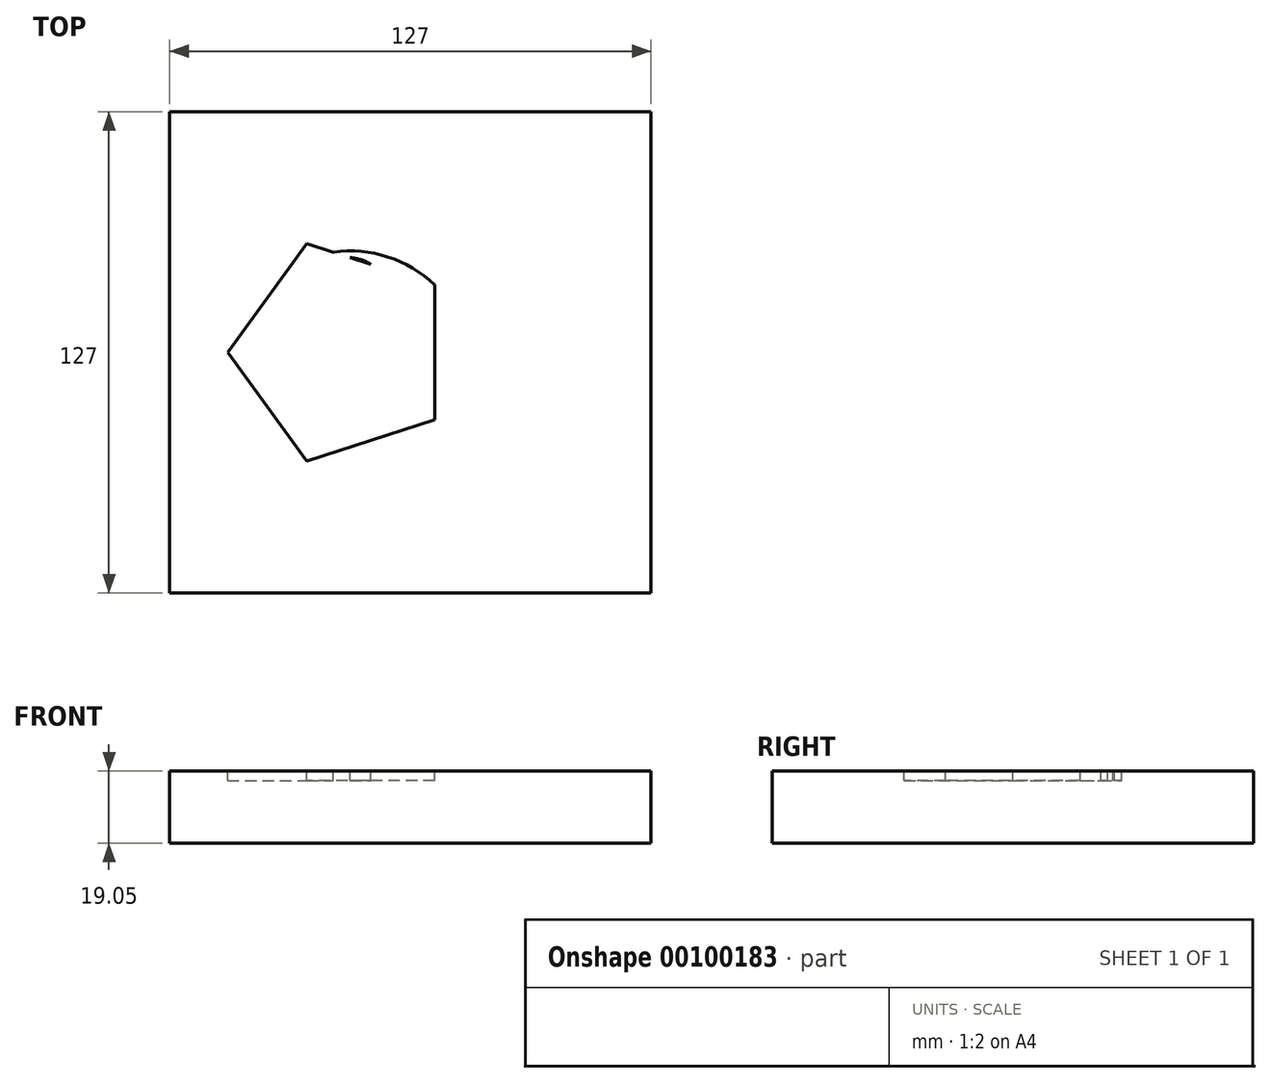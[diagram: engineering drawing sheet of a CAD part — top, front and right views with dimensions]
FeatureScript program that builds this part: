
annotation { "Feature Type Name" : "Feature", "Feature Type Description" : "" }
export const myFeature = defineFeature(function(context is Context, id is Id, definition is map)
    precondition{}
    {
        {
            var Q0;
            Q0=qCreatedBy(makeId("Top.planeOp"),FACE);
            var sketch = newSketch(context, id + "F0", { "sketchPlane" : qUnion([Q0])});
            skLineSegment(sketch, "E0.bottom", {"start": v(-63.5, -63.5) * mm, "end": v(63.5, -63.5) * mm});
            skLineSegment(sketch, "E0.top", {"start": v(-63.5, 63.5) * mm, "end": v(63.5, 63.5) * mm});
            skLineSegment(sketch, "E0.left", {"start": v(-63.5, -63.5) * mm, "end": v(-63.5, 63.5) * mm});
            skLineSegment(sketch, "E0.right", {"start": v(63.5, -63.5) * mm, "end": v(63.5, 63.5) * mm});
            skPoint(sketch, "E0.middle", {"position": v(0, 0) * mm});
            skSolve(sketch);
        }
        {
            var Q0;
            Q0 = qSketchRegion(id + "F0", true);
            extrude(context, id + "F1", {"entities" : qUnion([Q0]), "depth" : 19.05 * mm});
        }
        {
            var Q0;
            Q0=makeQuery(id+"F1.opExtrude","CAP_FACE",FACE,{"disambiguationData":[OSD([sQuery(id+"F0.wireOp",EDGE,"E0.bottom"),sQuery(id+"F0.wireOp",EDGE,"E0.top"),sQuery(id+"F0.wireOp",EDGE,"E0.left"),sQuery(id+"F0.wireOp",EDGE,"E0.right")])],"isStart":false});
            var sketch = newSketch(context, id + "F2", { "sketchPlane" : qUnion([Q0])});
            skCircle(sketch, "E1.cCircle", {"center": v(-18.01, 0) * mm, "radius": 24.42 * mm, "construction": true});
            skLineSegment(sketch, "E1.0", {"start": v(6.41, 17.74) * mm, "end": v(6.41, -17.74) * mm});
            skLineSegment(sketch, "E1.1", {"start": v(6.41, -17.74) * mm, "end": v(-27.34, -28.71) * mm});
            skLineSegment(sketch, "E1.2", {"start": v(-27.34, -28.71) * mm, "end": v(-48.2, 0) * mm});
            skLineSegment(sketch, "E1.3", {"start": v(-48.2, 0) * mm, "end": v(-27.34, 28.71) * mm});
            skLineSegment(sketch, "E1.4", {"start": v(-27.34, 28.71) * mm, "end": v(6.41, 17.74) * mm});
            skPoint(sketch, "E1.0.midPoint", {"position": v(6.41, 0) * mm});
            skArc(sketch, "E2", {"start": v(-10.47, 23.23) * mm, "mid": v(-20.3, 24.38) * mm, "end": v(-27.34, 17.4) * mm});
            skArc(sketch, "E3", {"start": v(6.41, 17.74) * mm, "mid": v(-5.95, 25.17) * mm, "end": v(-20.3, 26.43) * mm});
            skPoint(sketch, "E3.endSnap0", {"position": v(-20.3, 24.38) * mm});
            skSolve(sketch);
        }
        {
            var Q0;
            Q0 = qSketchRegion(id + "F2", true);
            extrude(context, id + "F3", {"entities" : qUnion([Q0]), "operationType" : NewBodyOperationType.REMOVE, "oppositeDirection" : true, "depth" : 2.54 * mm});
        }
    });
